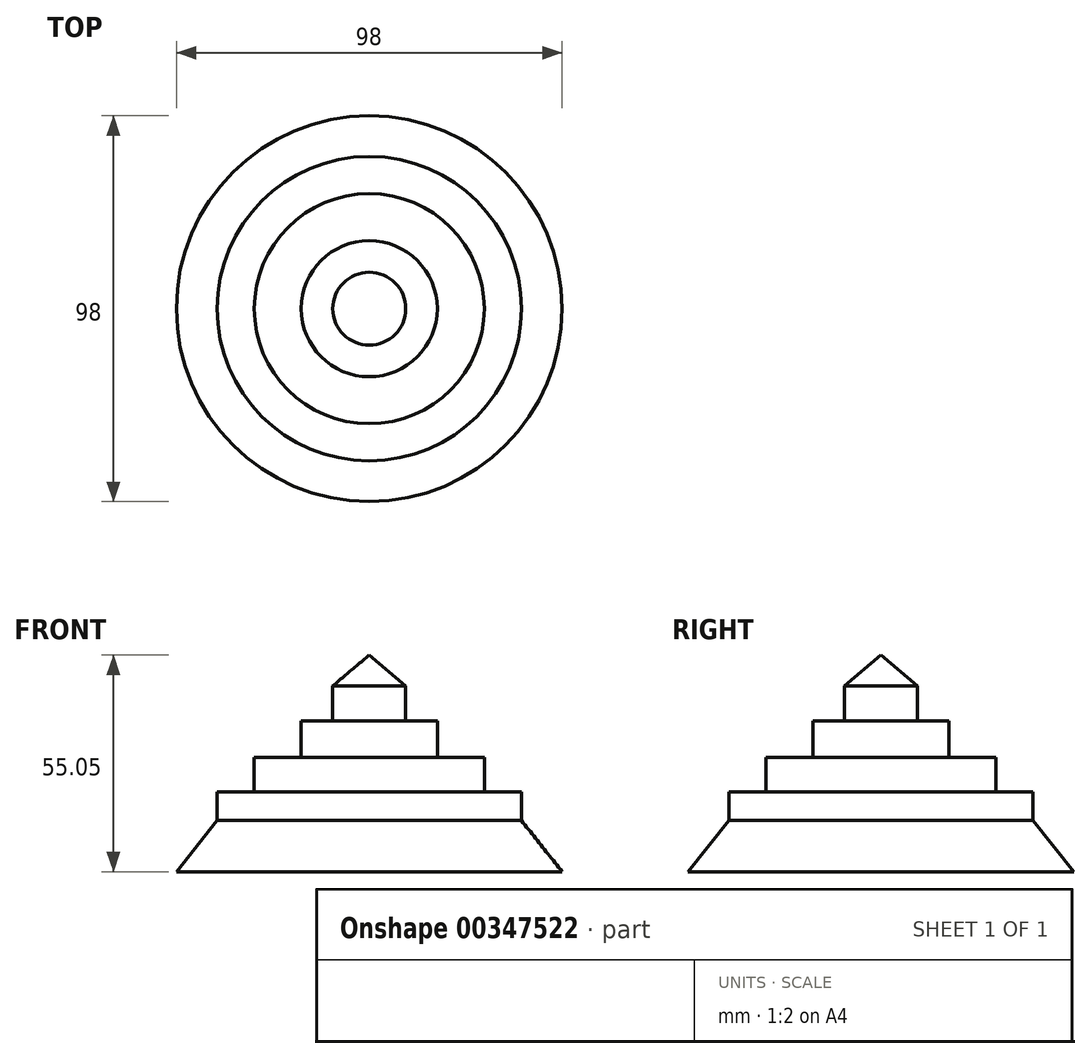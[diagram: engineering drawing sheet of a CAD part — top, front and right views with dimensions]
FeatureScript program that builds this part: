
annotation { "Feature Type Name" : "Feature", "Feature Type Description" : "" }
export const myFeature = defineFeature(function(context is Context, id is Id, definition is map)
    precondition{}
    {
        {
            var Q0;
            Q0=qCreatedBy(makeId("Right.planeOp"),FACE);
            var sketch = newSketch(context, id + "F0", { "sketchPlane" : qUnion([Q0])});
            skLineSegment(sketch, "E0", {"start": v(0, 55.05) * mm, "end": v(9.26, 47.21) * mm});
            skLineSegment(sketch, "E1", {"start": v(9.26, 47.21) * mm, "end": v(9.26, 38.3) * mm});
            skLineSegment(sketch, "E2", {"start": v(9.26, 38.3) * mm, "end": v(17.28, 38.3) * mm});
            skLineSegment(sketch, "E3", {"start": v(17.28, 38.3) * mm, "end": v(17.28, 29.04) * mm});
            skLineSegment(sketch, "E4", {"start": v(17.28, 29.04) * mm, "end": v(29.22, 29.04) * mm});
            skLineSegment(sketch, "E5", {"start": v(29.22, 29.04) * mm, "end": v(29.22, 20.31) * mm});
            skLineSegment(sketch, "E6", {"start": v(29.22, 20.31) * mm, "end": v(38.66, 20.31) * mm});
            skLineSegment(sketch, "E7", {"start": v(38.66, 20.31) * mm, "end": v(38.66, 13) * mm});
            skLineSegment(sketch, "E8", {"start": v(38.66, 13) * mm, "end": v(49, 0) * mm});
            skLineSegment(sketch, "E9", {"start": v(49, 0) * mm, "end": v(0, 0) * mm});
            skLineSegment(sketch, "E10", {"start": v(0, 55.05) * mm, "end": v(0, 0) * mm, "construction": true});
            skLineSegment(sketch, "E11", {"start": v(0, 55.05) * mm, "end": v(0, 0) * mm});
            skSolve(sketch);
        }
        {
            var Q0;
            Q0 = qSketchRegion(id + "F0", true);
            var Q1;
            Q1=sQuery(id+"F0.wireOp",EDGE,"E11");
            revolve(context, id + "F1", {"entities" : qUnion([Q0]), "axis" : qUnion([Q1]), "revolveType" : RevolveType.FULL});
        }
    });
